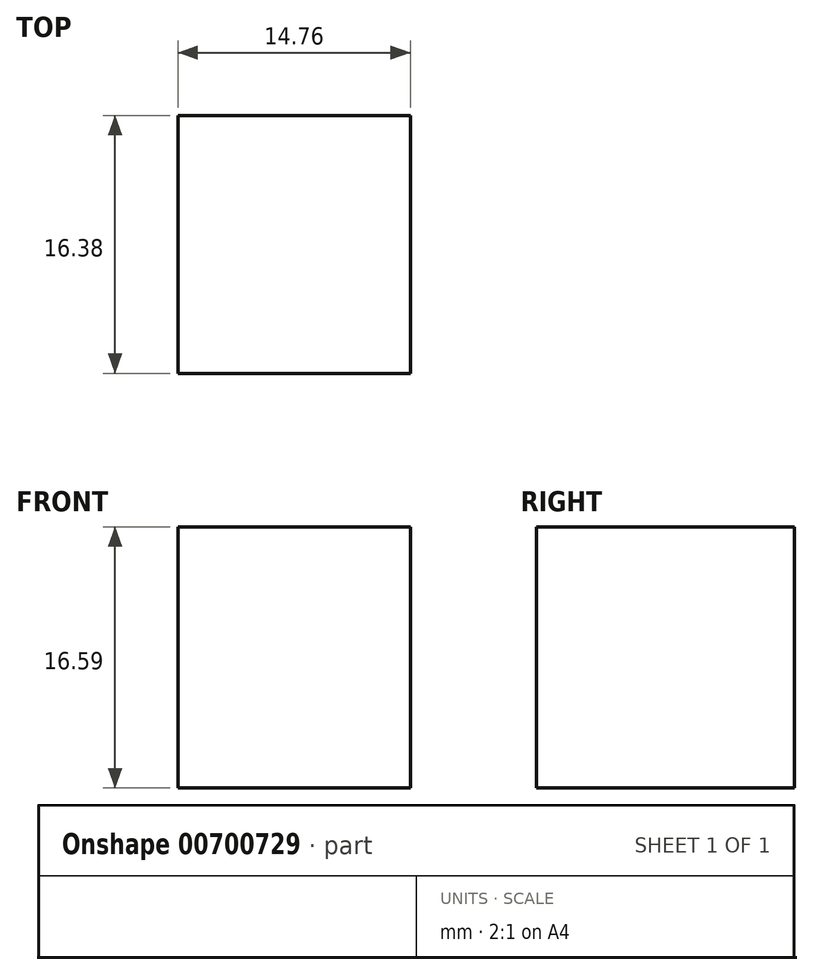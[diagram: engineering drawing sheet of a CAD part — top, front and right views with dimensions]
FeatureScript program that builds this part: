
annotation { "Feature Type Name" : "Feature", "Feature Type Description" : "" }
export const myFeature = defineFeature(function(context is Context, id is Id, definition is map)
    precondition{}
    {
        {
            var Q0;
            Q0=qCreatedBy(makeId("Top.planeOp"),FACE);
            var sketch = newSketch(context, id + "F0", { "sketchPlane" : qUnion([Q0])});
            skLineSegment(sketch, "E0.bottom", {"start": v(-32.92, 34.4) * mm, "end": v(-18.16, 34.4) * mm});
            skLineSegment(sketch, "E0.top", {"start": v(-32.92, 18) * mm, "end": v(-18.16, 18) * mm});
            skLineSegment(sketch, "E0.left", {"start": v(-32.92, 34.4) * mm, "end": v(-32.92, 18) * mm});
            skLineSegment(sketch, "E0.right", {"start": v(-18.16, 34.4) * mm, "end": v(-18.16, 18) * mm});
            skSolve(sketch);
        }
        {
            var Q0;
            Q0=makeQuery(id+"F0.imprint","IMPRINT",FACE,{"disambiguationData":[TD([[makeQuery(id+"F0.imprint","IMPRINT",EDGE,{"derivedFrom":sQuery(id+"F0.wireOp",EDGE,"E0.bottom")}),-1.0]])]});
            extrude(context, id + "F1", {"entities" : qUnion([Q0]), "depth" : 16.6 * mm, "offsetDistance" : 25 * mm});
        }
    });
